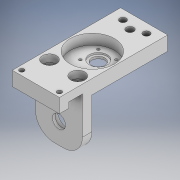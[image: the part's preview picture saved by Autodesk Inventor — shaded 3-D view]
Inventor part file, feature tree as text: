
AUTODESK INVENTOR PART (.ipt)
format: ipt  version: 2020 (Build 240168000, 168)  size: 240,640 bytes
history: native  units: mm
features: extrude x6, sketch x5, projected_geometry x5, other x1, fillet x1
ambient origin geometry x8: Origin, YZ Plane, XZ Plane, XY Plane, X Axis, Y Axis, Z Axis, Center Point
bodies: Solide1 (feature_tree), Solid1 (feature_tree)
feature tree (18):
  extrude  "Extrusion1"  Depth=1.0mm TaperAngle=0.0deg
  extrude  "Extrusion2"  Depth=1.0mm TaperAngle=0.0deg
  other  "Epaississement1"
  extrude  "Extrusion3"  Depth=1.0mm
  sketch  "Esquisse7"
  extrude  "Extrusion4"  Depth=1.0mm
  extrude  "Extrusion5"  Depth=10.0mm
  fillet  "Congé1"  Radius=53.8mm
  extrude  "Extrusion6"  Depth=31.8mm
  sketch  "Esquisse3"
  projected_geometry  "Boucle projetée1"
  sketch  "Esquisse4"
  projected_geometry  "Boucle projetée2"
  sketch  "Esquisse6"
  projected_geometry  "Boucle projetée3"
  sketch  "Esquisse10"
  projected_geometry  "Boucle projetée4"
  projected_geometry  "Boucle projetée5"
